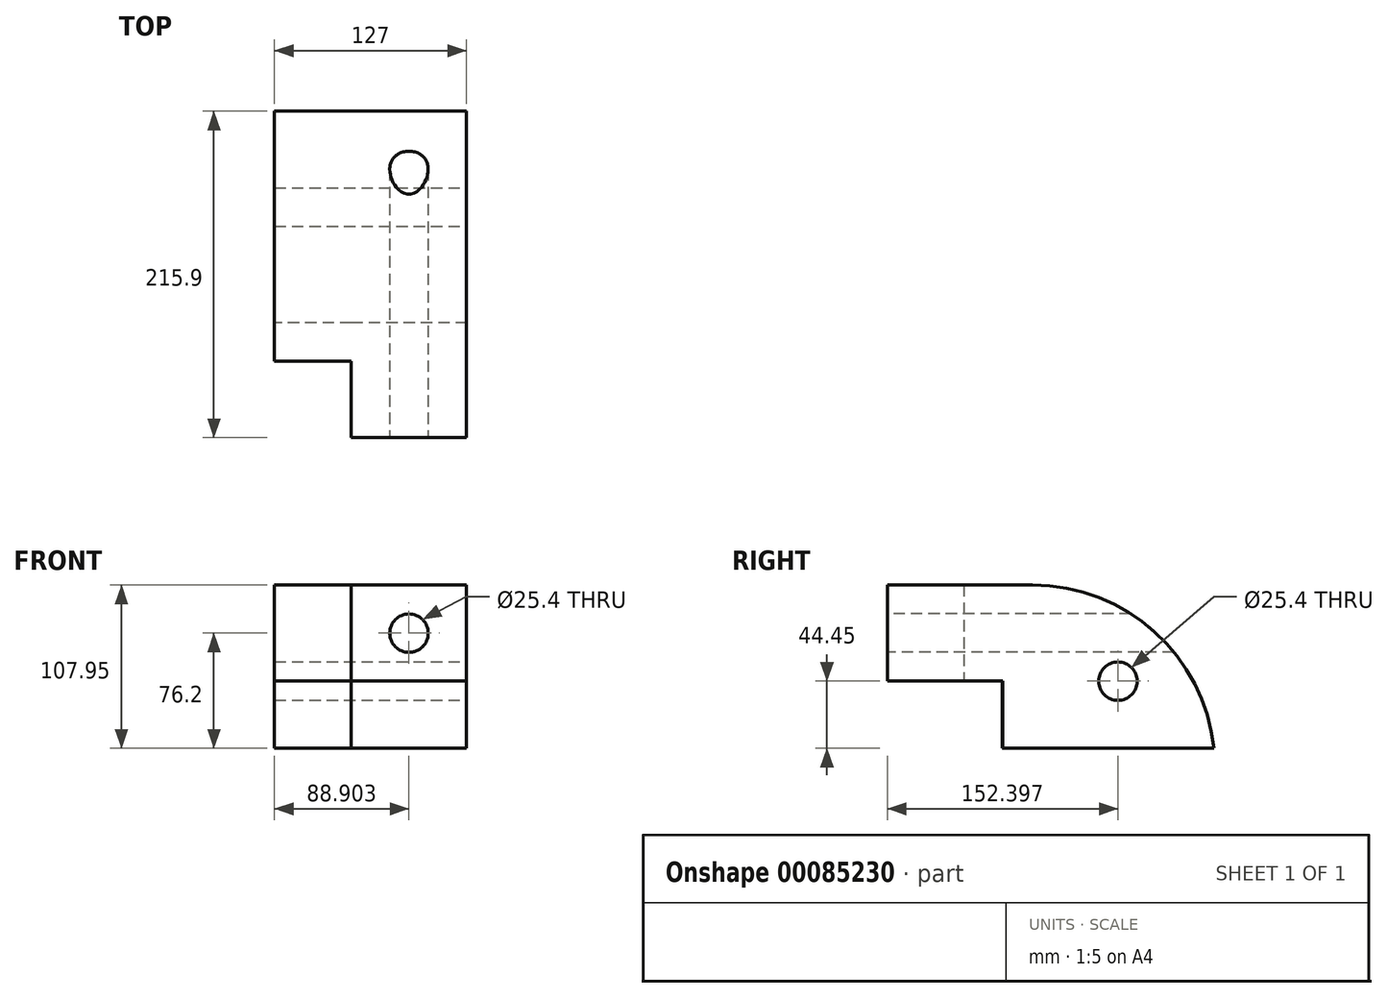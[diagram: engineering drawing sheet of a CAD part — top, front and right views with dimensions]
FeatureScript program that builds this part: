
annotation { "Feature Type Name" : "Feature", "Feature Type Description" : "" }
export const myFeature = defineFeature(function(context is Context, id is Id, definition is map)
    precondition{}
    {
        {
            var Q0;
            Q0=qCreatedBy(makeId("Top.planeOp"),FACE);
            var sketch = newSketch(context, id + "F0", { "sketchPlane" : qUnion([Q0])});
            skLineSegment(sketch, "E0.bottom", {"start": v(-80.34, 165.42) * mm, "end": v(46.66, 165.42) * mm});
            skLineSegment(sketch, "E0.top", {"start": v(-80.34, -50.48) * mm, "end": v(46.66, -50.48) * mm});
            skLineSegment(sketch, "E0.left", {"start": v(-80.34, 165.42) * mm, "end": v(-80.34, -50.48) * mm});
            skLineSegment(sketch, "E0.right", {"start": v(46.66, 165.42) * mm, "end": v(46.66, -50.48) * mm});
            skSolve(sketch);
        }
        {
            var Q0;
            Q0=makeQuery(id+"F0.imprint","IMPRINT",FACE,{"disambiguationData":[TD([[makeQuery(id+"F0.imprint","IMPRINT",EDGE,{"derivedFrom":sQuery(id+"F0.wireOp",EDGE,"E0.bottom")}),-1.0]])]});
            extrude(context, id + "F1", {"entities" : qUnion([Q0]), "depth" : 107.95 * mm});
        }
        {
            var Q0;
            Q0=makeQuery(id+"F1.opExtrude","SWEPT_FACE",FACE,{"disambiguationData":[OSD([sQuery(id+"F0.wireOp",EDGE,"E0.left")])]});
            var sketch = newSketch(context, id + "F2", { "sketchPlane" : qUnion([Q0])});
            skLineSegment(sketch, "E1.bottom", {"start": v(0, 107.95) * mm, "end": v(50.48, 107.95) * mm});
            skLineSegment(sketch, "E1.top", {"start": v(0, 0) * mm, "end": v(50.48, 0) * mm});
            skLineSegment(sketch, "E1.left", {"start": v(0, 107.95) * mm, "end": v(0, 0) * mm});
            skLineSegment(sketch, "E1.right", {"start": v(50.48, 107.95) * mm, "end": v(50.48, 0) * mm});
            skSolve(sketch);
        }
        {
            var Q0;
            Q0=makeQuery(id+"F2.imprint","IMPRINT",FACE,{"disambiguationData":[TD([[makeQuery(id+"F2.imprint","IMPRINT",EDGE,{"derivedFrom":sQuery(id+"F2.wireOp",EDGE,"E1.bottom")}),-1.0]])]});
            extrude(context, id + "F3", {"entities" : qUnion([Q0]), "operationType" : NewBodyOperationType.REMOVE, "oppositeDirection" : true, "depth" : 50.8 * mm});
        }
        {
            var Q0;
            Q0=makeQuery(id+"F1.opExtrude","SWEPT_FACE",FACE,{"disambiguationData":[OSD([sQuery(id+"F0.wireOp",EDGE,"E0.top")])]});
            var sketch = newSketch(context, id + "F4", { "sketchPlane" : qUnion([Q0])});
            skLineSegment(sketch, "E2.bottom", {"start": v(-29.54, 107.95) * mm, "end": v(46.66, 107.95) * mm});
            skLineSegment(sketch, "E2.top", {"start": v(-29.54, 44.45) * mm, "end": v(46.66, 44.45) * mm});
            skLineSegment(sketch, "E2.left", {"start": v(-29.54, 107.95) * mm, "end": v(-29.54, 44.45) * mm});
            skLineSegment(sketch, "E2.right", {"start": v(46.66, 107.95) * mm, "end": v(46.66, 44.45) * mm});
            skSolve(sketch);
        }
        {
            var Q0;
            {var subQ0=sQuery(id+"F4.wireOp",EDGE,"E2.top");Q0=makeQuery(id+"F4.imprint","IMPRINT",FACE,{"disambiguationData":[TD([[makeQuery(id+"F4.imprint","IMPRINT",EDGE,{"derivedFrom":subQ0}),-1.0]])]});}
            extrude(context, id + "F5", {"entities" : qUnion([Q0]), "operationType" : NewBodyOperationType.REMOVE, "oppositeDirection" : true, "depth" : 76.2 * mm});
        }
        {
            var Q0;
            Q0=makeQuery(id+"F1.opExtrude","SWEPT_FACE",FACE,{"disambiguationData":[OSD([sQuery(id+"F0.wireOp",EDGE,"E0.top")])]});
            var sketch = newSketch(context, id + "F6", { "sketchPlane" : qUnion([Q0])});
            skCircle(sketch, "E3", {"center": v(8.56, 76.2) * mm, "radius": 12.7 * mm});
            skSolve(sketch);
        }
        {
            var Q0;
            Q0=makeQuery(id+"F1.opExtrude","SWEPT_FACE",FACE,{"disambiguationData":[OSD([sQuery(id+"F0.wireOp",EDGE,"E0.right")])]});
            var sketch = newSketch(context, id + "F7", { "sketchPlane" : qUnion([Q0])});
            skCircle(sketch, "E4", {"center": v(101.92, 44.45) * mm, "radius": 12.7 * mm});
            skSolve(sketch);
        }
        {
            var Q0;
            Q0=makeQuery(id+"F1.opExtrude","CAP_EDGE",EDGE,{"disambiguationData":[OSD([sQuery(id+"F0.wireOp",EDGE,"E0.bottom")])],"isStart":false});
            fillet(context, id + "F8", {"entities" : qUnion([Q0]), "radius" : 120.65 * mm, "tangentPropagation" : true, "allowEdgeOverflow" : false});
        }
        {
            var Q0;
            Q0=makeQuery(id+"F6.imprint","IMPRINT",FACE,{"disambiguationData":[TD([[makeQuery(id+"F6.imprint","IMPRINT",EDGE,{"derivedFrom":sQuery(id+"F6.wireOp",EDGE,"E3")}),1.0]])]});
            extrude(context, id + "F9", {"entities" : qUnion([Q0]), "operationType" : NewBodyOperationType.REMOVE, "endBound" : BoundingType.THROUGH_ALL, "oppositeDirection" : true, "depth" : 25.4 * mm});
        }
        {
            var Q0;
            Q0=makeQuery(id+"F7.imprint","IMPRINT",FACE,{"disambiguationData":[TD([[makeQuery(id+"F7.imprint","IMPRINT",EDGE,{"derivedFrom":sQuery(id+"F7.wireOp",EDGE,"E4")}),1.0]])]});
            extrude(context, id + "F10", {"entities" : qUnion([Q0]), "operationType" : NewBodyOperationType.REMOVE, "oppositeDirection" : true, "depth" : 127 * mm});
        }
        {
            var Q0;
            Q0=makeQuery(id+"F1.opExtrude","SWEPT_FACE",FACE,{"disambiguationData":[OSD([sQuery(id+"F0.wireOp",EDGE,"E0.left")])]});
            var sketch = newSketch(context, id + "F11", { "sketchPlane" : qUnion([Q0])});
            skLineSegment(sketch, "E5.bottom", {"start": v(0, 0) * mm, "end": v(-25.4, 0) * mm});
            skLineSegment(sketch, "E5.top", {"start": v(0, 44.45) * mm, "end": v(-25.4, 44.45) * mm});
            skLineSegment(sketch, "E5.left", {"start": v(0, 0) * mm, "end": v(0, 44.45) * mm});
            skLineSegment(sketch, "E5.right", {"start": v(-25.4, 0) * mm, "end": v(-25.4, 44.45) * mm});
            skSolve(sketch);
        }
        {
            var Q0;
            Q0 = qSketchRegion(id + "F11", true);
            extrude(context, id + "F12", {"entities" : qUnion([Q0]), "operationType" : NewBodyOperationType.REMOVE, "oppositeDirection" : true, "depth" : 50.8 * mm});
        }
    });
